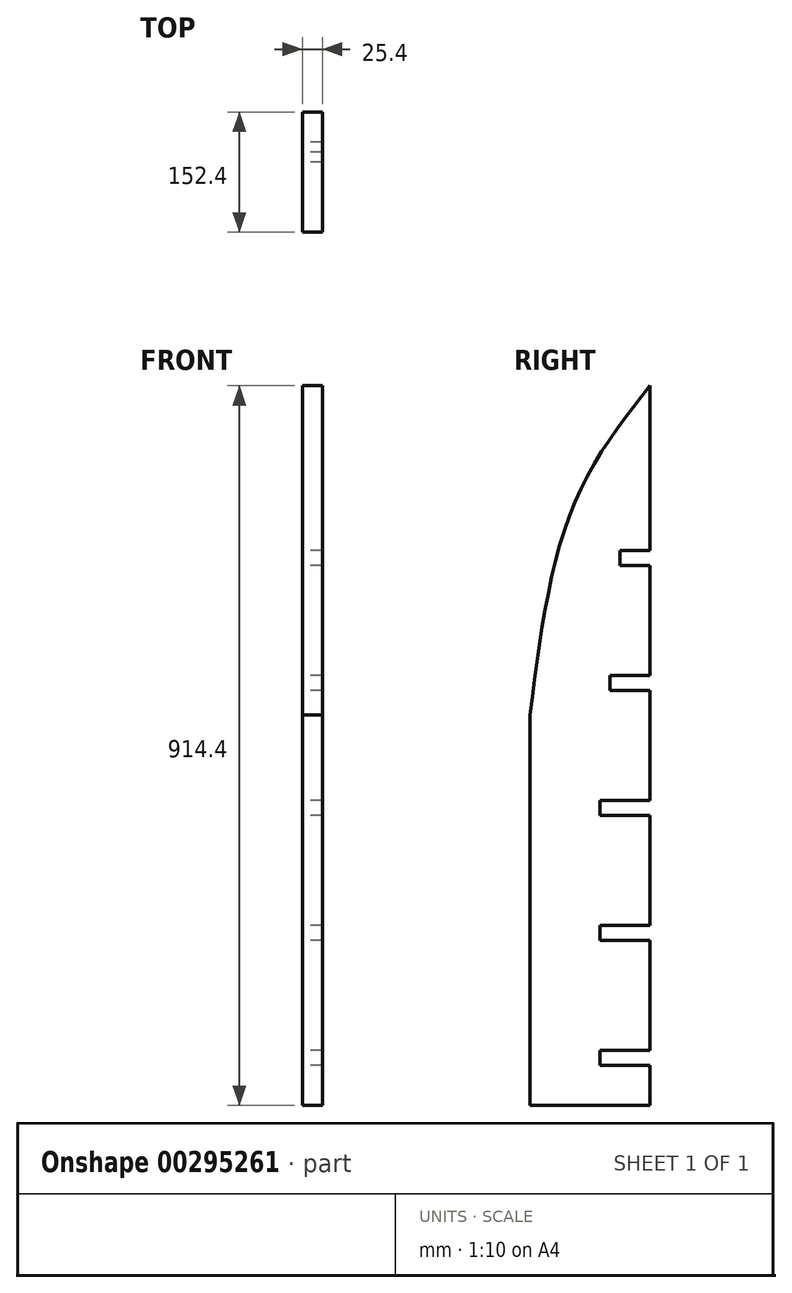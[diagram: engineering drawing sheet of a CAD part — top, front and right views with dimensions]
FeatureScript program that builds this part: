
annotation { "Feature Type Name" : "Feature", "Feature Type Description" : "" }
export const myFeature = defineFeature(function(context is Context, id is Id, definition is map)
    precondition{}
    {
        {
            var Q0;
            Q0=qCreatedBy(makeId("Right.planeOp"),FACE);
            var sketch = newSketch(context, id + "F0", { "sketchPlane" : qUnion([Q0])});
            skLineSegment(sketch, "E0.bottom", {"start": v(76.2, -457.2) * mm, "end": v(-76.2, -457.2) * mm});
            skLineSegment(sketch, "E0.left", {"start": v(76.2, -457.2) * mm, "end": v(76.2, -406.4) * mm});
            skLineSegment(sketch, "E0.right", {"start": v(-76.2, -457.2) * mm, "end": v(-76.2, 39.03) * mm});
            skPoint(sketch, "E0.middle", {"position": v(0, 0) * mm});
            skFitSpline(sketch, "E1", {"points": [v(76.2, 457.2) * mm, v(-22.2, 301.87) * mm, v(-76.2, 39.03) * mm], "startDerivative": vector(-244.1, -311.85) * mm, "endDerivative": vector(-66.3, -518) * mm});
            skPoint(sketch, "E2.orphan", {"position": v(-76.2, 457.2) * mm});
            skLineSegment(sketch, "E3.bottom", {"start": v(76.2, -387.35) * mm, "end": v(12.7, -387.35) * mm});
            skLineSegment(sketch, "E3.top", {"start": v(76.2, -406.4) * mm, "end": v(12.7, -406.4) * mm});
            skLineSegment(sketch, "E3.right", {"start": v(12.7, -387.35) * mm, "end": v(12.7, -406.4) * mm});
            skLineSegment(sketch, "E4.bottom", {"start": v(76.2, -247.65) * mm, "end": v(12.7, -247.65) * mm});
            skLineSegment(sketch, "E4.top", {"start": v(76.2, -228.6) * mm, "end": v(12.7, -228.6) * mm});
            skLineSegment(sketch, "E4.right", {"start": v(12.7, -247.65) * mm, "end": v(12.7, -228.6) * mm});
            skLineSegment(sketch, "E5.bottom", {"start": v(76.2, -88.9) * mm, "end": v(12.7, -88.9) * mm});
            skLineSegment(sketch, "E5.top", {"start": v(76.2, -69.85) * mm, "end": v(12.7, -69.85) * mm});
            skLineSegment(sketch, "E5.right", {"start": v(12.7, -88.9) * mm, "end": v(12.7, -69.85) * mm});
            skLineSegment(sketch, "E6.bottom", {"start": v(76.2, 69.85) * mm, "end": v(25.4, 69.85) * mm});
            skLineSegment(sketch, "E6.top", {"start": v(76.2, 88.9) * mm, "end": v(25.4, 88.9) * mm});
            skLineSegment(sketch, "E6.right", {"start": v(25.4, 69.85) * mm, "end": v(25.4, 88.9) * mm});
            skLineSegment(sketch, "E7.bottom", {"start": v(76.2, 228.6) * mm, "end": v(38.1, 228.6) * mm});
            skLineSegment(sketch, "E7.top", {"start": v(76.2, 247.65) * mm, "end": v(38.1, 247.65) * mm});
            skLineSegment(sketch, "E7.right", {"start": v(38.1, 228.6) * mm, "end": v(38.1, 247.65) * mm});
            skLineSegment(sketch, "E8.trimOffspring", {"start": v(76.2, 247.65) * mm, "end": v(76.2, 457.2) * mm});
            skLineSegment(sketch, "E9.trimOffspring", {"start": v(76.2, 88.9) * mm, "end": v(76.2, 228.6) * mm});
            skLineSegment(sketch, "E10.trimOffspring", {"start": v(76.2, -69.85) * mm, "end": v(76.2, 69.85) * mm});
            skLineSegment(sketch, "E11.trimOffspring", {"start": v(76.2, -228.6) * mm, "end": v(76.2, -88.9) * mm});
            skLineSegment(sketch, "E12.trimOffspring", {"start": v(76.2, -387.35) * mm, "end": v(76.2, -247.65) * mm});
            skSolve(sketch);
        }
        {
            var Q0;
            Q0=makeQuery(id+"F0.imprint","IMPRINT",FACE,{"disambiguationData":[TD([[makeQuery(id+"F0.imprint","IMPRINT",EDGE,{"derivedFrom":sQuery(id+"F0.wireOp",EDGE,"E0.bottom")}),-1.0]])]});
            extrude(context, id + "F1", {"entities" : qUnion([Q0]), "depth" : 25.4 * mm});
        }
    });
